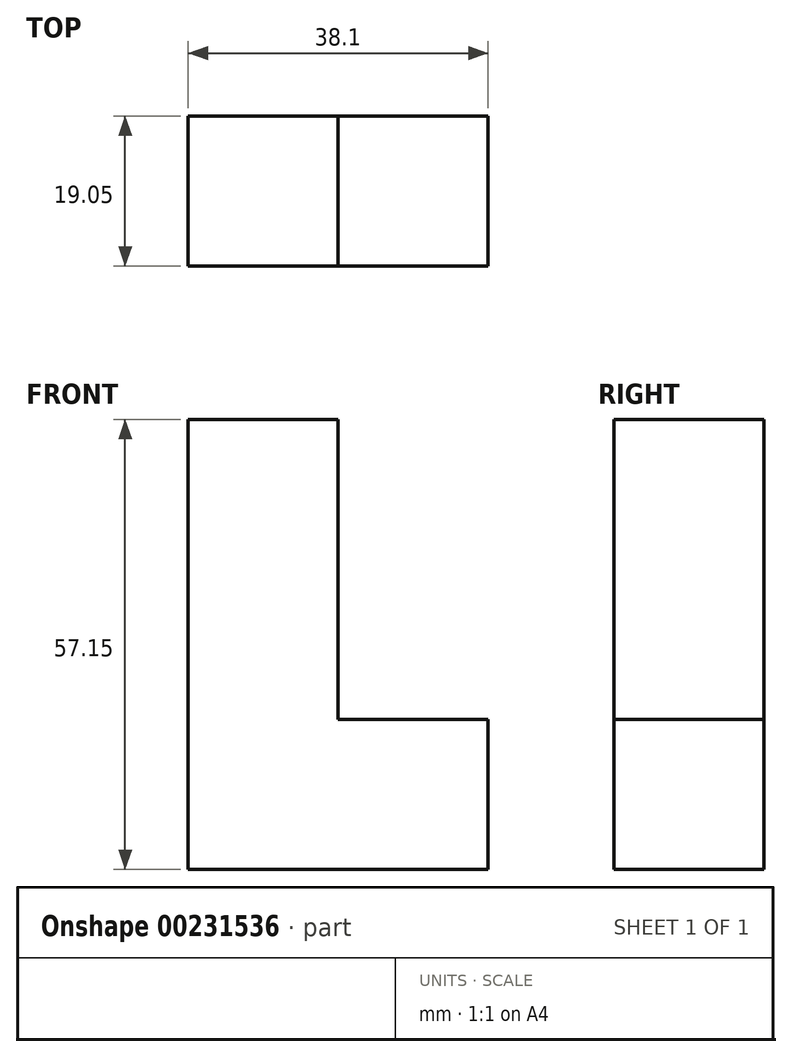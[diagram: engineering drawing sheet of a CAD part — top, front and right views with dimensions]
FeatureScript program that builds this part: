
annotation { "Feature Type Name" : "Feature", "Feature Type Description" : "" }
export const myFeature = defineFeature(function(context is Context, id is Id, definition is map)
    precondition{}
    {
        {
            var Q0;
            Q0=qCreatedBy(makeId("Front.planeOp"),FACE);
            var sketch = newSketch(context, id + "F0", { "sketchPlane" : qUnion([Q0])});
            skLineSegment(sketch, "E0.bottom", {"start": v(-49, 47.34) * mm, "end": v(-29.95, 47.34) * mm});
            skLineSegment(sketch, "E0.top", {"start": v(-49, -9.8) * mm, "end": v(-29.95, -9.8) * mm});
            skLineSegment(sketch, "E0.left", {"start": v(-49, 47.34) * mm, "end": v(-49, -9.8) * mm});
            skLineSegment(sketch, "E0.right", {"start": v(-29.95, 47.34) * mm, "end": v(-29.95, -9.8) * mm});
            skLineSegment(sketch, "E1.bottom", {"start": v(-29.95, 9.24) * mm, "end": v(-10.9, 9.24) * mm});
            skLineSegment(sketch, "E1.top", {"start": v(-29.95, -9.8) * mm, "end": v(-10.9, -9.8) * mm});
            skLineSegment(sketch, "E1.left", {"start": v(-29.95, 9.24) * mm, "end": v(-29.95, -9.8) * mm});
            skLineSegment(sketch, "E1.right", {"start": v(-10.9, 9.24) * mm, "end": v(-10.9, -9.8) * mm});
            skSolve(sketch);
        }
        {
            var Q0;
            Q0=makeQuery(id+"F0.imprint","IMPRINT",FACE,{"disambiguationData":[TD([[makeQuery(id+"F0.imprint","IMPRINT",EDGE,{"derivedFrom":sQuery(id+"F0.wireOp",EDGE,"E0.bottom")}),-1.0]])]});
            var Q1;
            Q1=makeQuery(id+"F0.imprint","IMPRINT",FACE,{"disambiguationData":[TD([[makeQuery(id+"F0.imprint","IMPRINT",EDGE,{"derivedFrom":sQuery(id+"F0.wireOp",EDGE,"E1.bottom")}),-1.0]])]});
            extrude(context, id + "F1", {"entities" : qUnion([Q0, Q1]), "depth" : 19.05 * mm});
        }
    });
